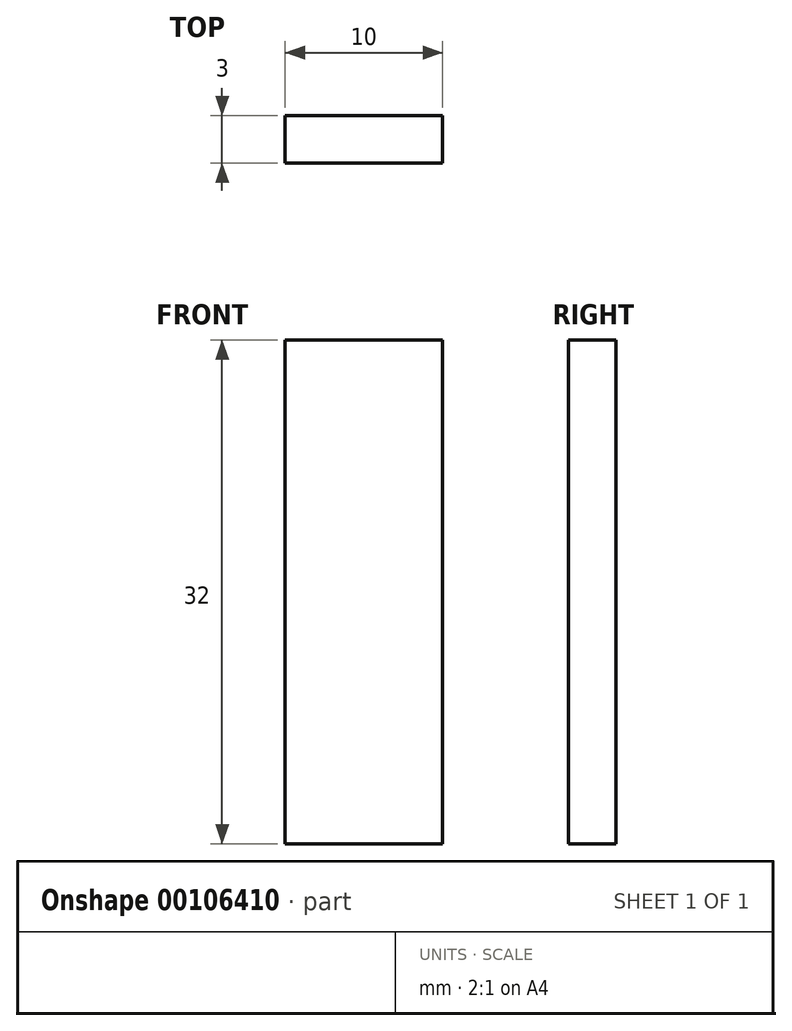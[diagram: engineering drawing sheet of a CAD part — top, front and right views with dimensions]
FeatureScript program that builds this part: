
annotation { "Feature Type Name" : "Feature", "Feature Type Description" : "" }
export const myFeature = defineFeature(function(context is Context, id is Id, definition is map)
    precondition{}
    {
        {
            var Q0;
            Q0=qCreatedBy(makeId("Top.planeOp"),FACE);
            var sketch = newSketch(context, id + "F0", { "sketchPlane" : qUnion([Q0])});
            skLineSegment(sketch, "E0.bottom", {"start": v(5, -1.5) * mm, "end": v(-5, -1.5) * mm});
            skLineSegment(sketch, "E0.top", {"start": v(5, 1.5) * mm, "end": v(-5, 1.5) * mm});
            skLineSegment(sketch, "E0.left", {"start": v(5, -1.5) * mm, "end": v(5, 1.5) * mm});
            skLineSegment(sketch, "E0.right", {"start": v(-5, -1.5) * mm, "end": v(-5, 1.5) * mm});
            skPoint(sketch, "E0.middle", {"position": v(0, 0) * mm});
            skSolve(sketch);
        }
        {
            var Q0;
            Q0=makeQuery(id+"F0.imprint","IMPRINT",FACE,{"disambiguationData":[TD([[makeQuery(id+"F0.imprint","IMPRINT",EDGE,{"derivedFrom":sQuery(id+"F0.wireOp",EDGE,"E0.bottom")}),-1.0]])]});
            extrude(context, id + "F1", {"entities" : qUnion([Q0]), "depth" : 32 * mm, "symmetric" : true});
        }
    });
